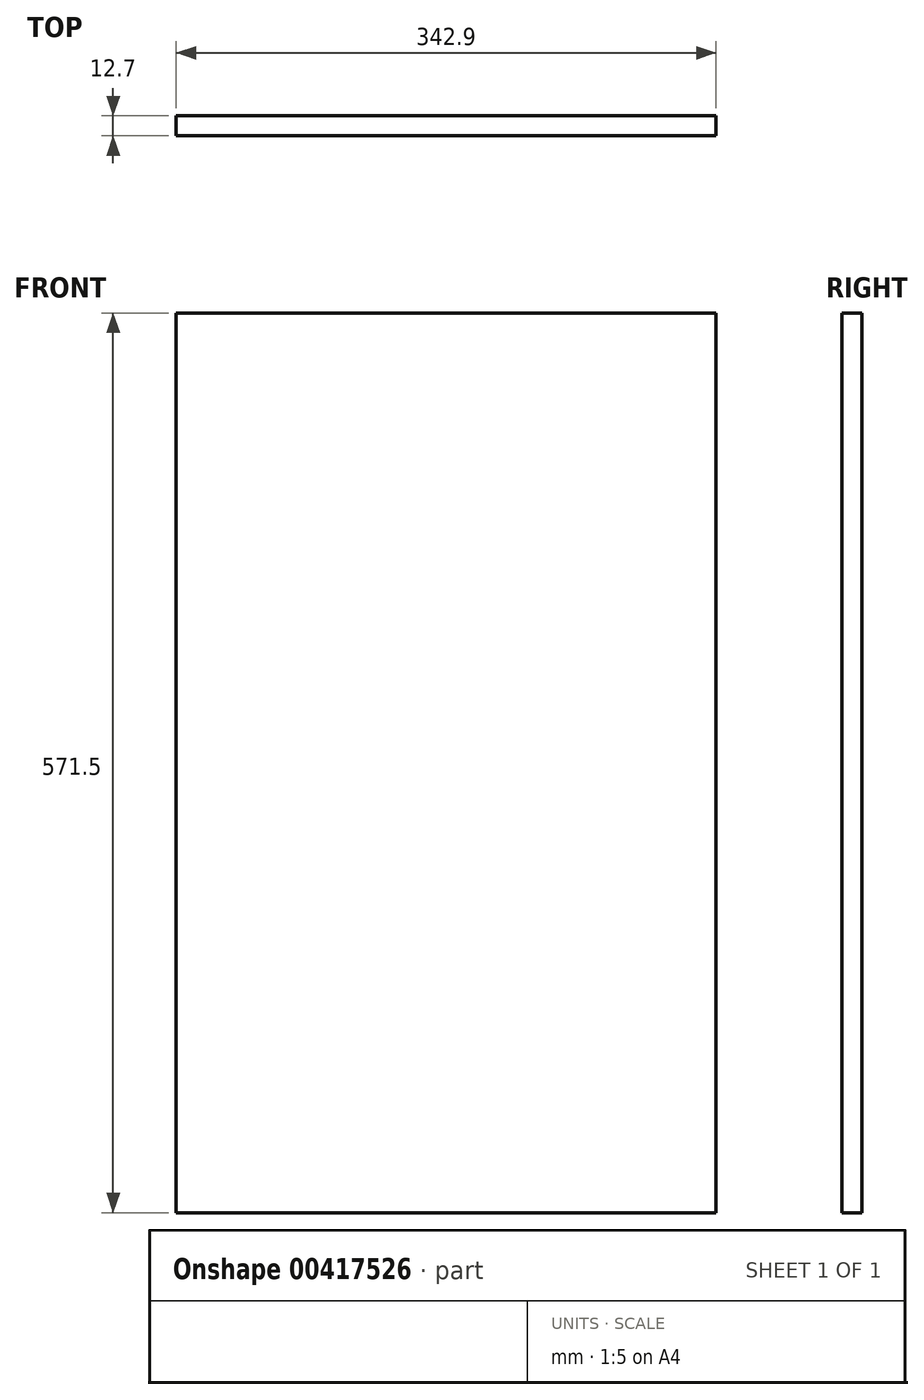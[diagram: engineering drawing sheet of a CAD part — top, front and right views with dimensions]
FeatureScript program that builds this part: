
annotation { "Feature Type Name" : "Feature", "Feature Type Description" : "" }
export const myFeature = defineFeature(function(context is Context, id is Id, definition is map)
    precondition{}
    {
        {
            var Q0;
            Q0=qCreatedBy(makeId("Front.planeOp"),FACE);
            var sketch = newSketch(context, id + "F0", { "sketchPlane" : qUnion([Q0])});
            skLineSegment(sketch, "E0.bottom", {"start": v(-171.45, 285.75) * mm, "end": v(171.45, 285.75) * mm});
            skLineSegment(sketch, "E0.top", {"start": v(-171.45, -285.75) * mm, "end": v(171.45, -285.75) * mm});
            skLineSegment(sketch, "E0.left", {"start": v(-171.45, 285.75) * mm, "end": v(-171.45, -285.75) * mm});
            skLineSegment(sketch, "E0.right", {"start": v(171.45, 285.75) * mm, "end": v(171.45, -285.75) * mm});
            skPoint(sketch, "E0.middle", {"position": v(0, 0) * mm});
            skSolve(sketch);
        }
        {
            var Q0;
            Q0=makeQuery(id+"F0.imprint","IMPRINT",FACE,{"disambiguationData":[TD([[makeQuery(id+"F0.imprint","IMPRINT",EDGE,{"derivedFrom":sQuery(id+"F0.wireOp",EDGE,"E0.bottom")}),-1.0]])]});
            extrude(context, id + "F1", {"entities" : qUnion([Q0]), "depth" : 12.7 * mm});
        }
    });
